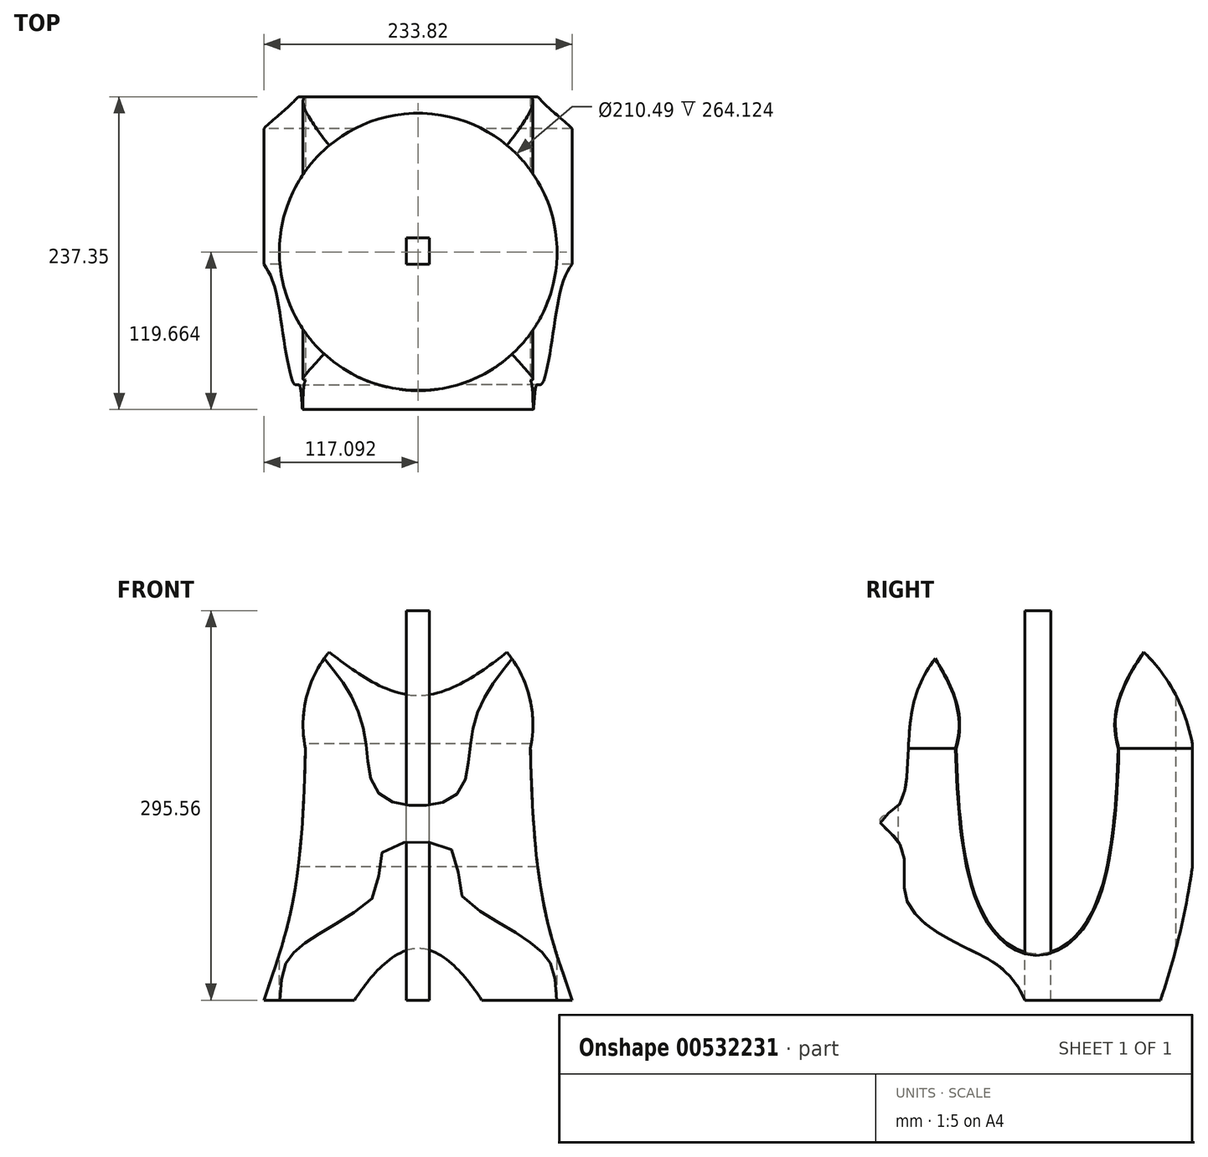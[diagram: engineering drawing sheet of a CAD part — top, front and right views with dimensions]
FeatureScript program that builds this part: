
annotation { "Feature Type Name" : "Feature", "Feature Type Description" : "" }
export const myFeature = defineFeature(function(context is Context, id is Id, definition is map)
    precondition{}
    {
        {
            var Q0;
            Q0=qCreatedBy(makeId("Front.planeOp"),FACE);
            var sketch = newSketch(context, id + "F0", { "sketchPlane" : qUnion([Q0])});
            skLineSegment(sketch, "E0.bottom", {"start": v(-122.26, 147.78) * mm, "end": v(122.26, 147.78) * mm});
            skLineSegment(sketch, "E0.top", {"start": v(-122.26, -147.78) * mm, "end": v(122.26, -147.78) * mm});
            skLineSegment(sketch, "E0.left", {"start": v(-122.26, 147.78) * mm, "end": v(-122.26, -147.78) * mm});
            skLineSegment(sketch, "E0.right", {"start": v(122.26, 147.78) * mm, "end": v(122.26, -147.78) * mm});
            skPoint(sketch, "E0.middle", {"position": v(0, 0) * mm});
            skSolve(sketch);
        }
        {
            var Q0;
            Q0=makeQuery(id+"F0.imprint","IMPRINT",FACE,{"disambiguationData":[TD([[makeQuery(id+"F0.imprint","IMPRINT",EDGE,{"derivedFrom":sQuery(id+"F0.wireOp",EDGE,"E0.bottom")}),-1.0]])]});
            var sketch = newSketch(context, id + "F1", { "sketchPlane" : qUnion([Q0])});
            skSolve(sketch);
        }
        {
            var Q0;
            Q0=makeQuery(id+"F1.imprint","IMPRINT",FACE,{"disambiguationData":[TD([[makeQuery(id+"F1.imprint","IMPRINT",EDGE,{"derivedFrom":makeQuery(id+"F0.imprint","IMPRINT",EDGE,{"derivedFrom":sQuery(id+"F0.wireOp",EDGE,"E0.bottom")})}),-1.0]])]});
            extrude(context, id + "F2", {"entities" : qUnion([Q0]), "depth" : 254 * mm, "offsetDistance" : 25.4 * mm});
        }
        {
            var Q0;
            Q0=makeQuery(id+"F2.opExtrude","SWEPT_FACE",FACE,{"disambiguationData":[OSD([sQuery(id+"F0.wireOp",EDGE,"E0.left")])]});
            var sketch = newSketch(context, id + "F3", { "sketchPlane" : qUnion([Q0])});
            skFitSpline(sketch, "E1", {"points": [v(127, 147.78) * mm, v(209.77, 83.15) * mm, v(222.75, 0) * mm, v(237.35, -11.05) * mm, v(221.13, -30.54) * mm, v(216.26, -72.76) * mm, v(167.59, -110.12) * mm, v(127, -147.78) * mm, v(82.57, -243.37) * mm, v(0, 46.73) * mm, v(127, 147.78) * mm]});
            skSolve(sketch);
        }
        {
            var Q0;
            Q0=makeQuery(id+"F2.opExtrude","CAP_FACE",FACE,{"disambiguationData":[OSD([sQuery(id+"F0.wireOp",EDGE,"E0.bottom"),sQuery(id+"F0.wireOp",EDGE,"E0.top"),sQuery(id+"F0.wireOp",EDGE,"E0.left"),sQuery(id+"F0.wireOp",EDGE,"E0.right")])],"isStart":false});
            var sketch = newSketch(context, id + "F4", { "sketchPlane" : qUnion([Q0])});
            skSolve(sketch);
        }
        {
            var Q0;
            Q0=makeQuery(id+"F4.imprint","IMPRINT",FACE,{"disambiguationData":[TD([[makeQuery(id+"F4.imprint","IMPRINT",EDGE,{"derivedFrom":makeQuery(id+"F2.opExtrude","CAP_EDGE",EDGE,{"disambiguationData":[OSD([sQuery(id+"F0.wireOp",EDGE,"E0.bottom")])],"isStart":false})}),-1.0]])]});
            var sketch = newSketch(context, id + "F5", { "sketchPlane" : qUnion([Q0])});
            skCircle(sketch, "E2", {"center": v(0, 61.09) * mm, "radius": 87.13 * mm});
            skFitSpline(sketch, "E3", {"points": [v(-85.3, 43.32) * mm, v(-113.26, -137.14) * mm, v(-161.96, -212.46) * mm, v(-253.92, -205.78) * mm], "startDerivative": vector(-15.24, -786.7) * mm, "endDerivative": vector(-205.06, 38.18) * mm});
            skLineSegment(sketch, "E4", {"start": v(0, -173.41) * mm, "end": v(0, 280.84) * mm});
            skFitSpline(sketch, "E5.MirrorCS", {"points": [v(85.3, 43.32) * mm, v(113.26, -137.14) * mm, v(161.96, -212.46) * mm, v(253.92, -205.78) * mm], "startDerivative": vector(15.24, -786.7) * mm, "endDerivative": vector(205.06, 38.18) * mm});
            skSolve(sketch);
        }
        {
            var Q0;
            {var subQ0=makeQuery(id+"F4.imprint","IMPRINT",EDGE,{"derivedFrom":makeQuery(id+"F2.opExtrude","CAP_EDGE",EDGE,{"disambiguationData":[OSD([sQuery(id+"F0.wireOp",EDGE,"E0.left")])],"isStart":false})});Q0=makeQuery(id+"F5.imprint","IMPRINT",FACE,{"disambiguationData":[TD([[makeQuery(id+"F5.imprint","IMPRINT",EDGE,{"derivedFrom":subQ0}),1.0]])]});}
            var Q1;
            {var subQ0=makeQuery(id+"F4.imprint","IMPRINT",EDGE,{"derivedFrom":makeQuery(id+"F2.opExtrude","CAP_EDGE",EDGE,{"disambiguationData":[OSD([sQuery(id+"F0.wireOp",EDGE,"E0.right")])],"isStart":false})});Q1=makeQuery(id+"F5.imprint","IMPRINT",FACE,{"disambiguationData":[TD([[makeQuery(id+"F5.imprint","IMPRINT",EDGE,{"derivedFrom":subQ0}),-1.0]])]});}
            extrude(context, id + "F6", {"entities" : qUnion([Q0, Q1]), "operationType" : NewBodyOperationType.REMOVE, "oppositeDirection" : true, "depth" : 304.8 * mm, "offsetDistance" : 25.4 * mm});
        }
        {
            var Q0;
            {var subQ1=sQuery(id+"F0.wireOp",EDGE,"E0.left");var subQ6=makeQuery(id+"F2.opExtrude","CAP_EDGE",EDGE,{"disambiguationData":[OSD([subQ1])],"isStart":false});Q0=makeQuery(id+"F3.imprint","IMPRINT",FACE,{"disambiguationData":[TD([[makeQuery(id+"F3.imprint","IMPRINT",EDGE,{"derivedFrom":subQ6}),-1.0]])]});}
            var Q1;
            {var subQ0=sQuery(id+"F3.wireOp",EDGE,"E1");var subQ1=sQuery(id+"F0.wireOp",EDGE,"E0.left");var subQ2=makeQuery(id+"F2.opExtrude","CAP_EDGE",EDGE,{"disambiguationData":[OSD([subQ1])],"isStart":true});var subQ3=makeQuery(id+"F3.imprint","INTERSECT",VERTEX,{"disambiguationData":[OD(1.0)],"derivedFrom":[subQ2,subQ0]});Q1=makeQuery(id+"F3.imprint","IMPRINT",FACE,{"disambiguationData":[TD([[makeQuery(id+"F3.imprint","IMPRINT",EDGE,{"disambiguationData":[TD([[subQ3,-1.0]])],"derivedFrom":subQ0}),1.0]])]});}
            var Q2;
            {var subQ0=sQuery(id+"F3.wireOp",EDGE,"E1");var subQ1=sQuery(id+"F0.wireOp",EDGE,"E0.left");var subQ4=makeQuery(id+"F2.opExtrude","CAP_EDGE",EDGE,{"disambiguationData":[OSD([subQ1])],"isStart":true});var subQ5=makeQuery(id+"F3.imprint","INTERSECT",VERTEX,{"disambiguationData":[OD(0.0)],"derivedFrom":[subQ4,subQ0]});Q2=makeQuery(id+"F3.imprint","IMPRINT",FACE,{"disambiguationData":[TD([[makeQuery(id+"F3.imprint","IMPRINT",EDGE,{"disambiguationData":[TD([[subQ5,1.0]])],"derivedFrom":subQ0}),1.0]])]});}
            extrude(context, id + "F7", {"entities" : qUnion([Q0, Q1, Q2]), "operationType" : NewBodyOperationType.REMOVE, "oppositeDirection" : true, "depth" : 304.8 * mm, "offsetDistance" : 25.4 * mm});
        }
        {
            var Q0;
            Q0=makeQuery(id+"F2.opExtrude","SWEPT_FACE",FACE,{"disambiguationData":[OSD([sQuery(id+"F0.wireOp",EDGE,"E0.bottom")])]});
            var sketch = newSketch(context, id + "F8", { "sketchPlane" : qUnion([Q0])});
            skCircle(sketch, "E6", {"center": v(0, -117.1) * mm, "radius": 154.42 * mm});
            skPoint(sketch, "E6.centerSnap0", {"position": v(8.74, -117.1) * mm});
            skCircle(sketch, "E7", {"center": v(0.18, -117.69) * mm, "radius": 105.25 * mm});
            skLineSegment(sketch, "E8.bottom", {"start": v(-190.87, 91.4) * mm, "end": v(195, 91.4) * mm});
            skLineSegment(sketch, "E8.top", {"start": v(-190.87, -331.5) * mm, "end": v(195, -331.5) * mm});
            skLineSegment(sketch, "E8.left", {"start": v(-190.87, 91.4) * mm, "end": v(-190.87, -331.5) * mm});
            skLineSegment(sketch, "E8.right", {"start": v(195, 91.4) * mm, "end": v(195, -331.5) * mm});
            skPoint(sketch, "E8.middle", {"position": v(2.07, -120.05) * mm});
            skSolve(sketch);
        }
        {
            var Q0;
            Q0=makeQuery(id+"F8.imprint","IMPRINT",FACE,{"disambiguationData":[TD([[makeQuery(id+"F8.imprint","IMPRINT",EDGE,{"derivedFrom":sQuery(id+"F8.wireOp",EDGE,"E7")}),1.0]])]});
            var Q1;
            Q1=makeQuery(id+"F8.imprint","IMPRINT",FACE,{"disambiguationData":[TD([[makeQuery(id+"F8.imprint","IMPRINT",EDGE,{"derivedFrom":sQuery(id+"F8.wireOp",EDGE,"E6")}),-1.0]])]});
            var Q2;
            {var subQ2=sQuery(id+"F0.wireOp",EDGE,"E0.bottom");var subQ4=sQuery(id+"F5.wireOp",EDGE,"E2");var subQ5=makeQuery(id+"F4.imprint","IMPRINT",EDGE,{"derivedFrom":makeQuery(id+"F2.opExtrude","CAP_EDGE",EDGE,{"disambiguationData":[OSD([subQ2])],"isStart":false})});Q2=makeQuery(id+"F8.imprint","IMPRINT",FACE,{"disambiguationData":[TD([[makeQuery(id+"F8.imprint","IMPRINT",EDGE,{"derivedFrom":makeQuery(id+"F6.boolean.opBoolean","COPY",EDGE,{"derivedFrom":makeQuery(id+"F6.opExtrude","SWEPT_EDGE",EDGE,{"disambiguationData":[OSD([subQ2,subQ4]),TDD([makeQuery(id+"F5.imprint","INTERSECT",VERTEX,{"disambiguationData":[OD(0.0)],"derivedFrom":[subQ5,subQ4]})])]})})}),-1.0]])]});}
            extrude(context, id + "F9", {"entities" : qUnion([Q0, Q1, Q2]), "operationType" : NewBodyOperationType.REMOVE, "oppositeDirection" : true, "depth" : 330.2 * mm, "offsetDistance" : 25.4 * mm});
        }
    });
